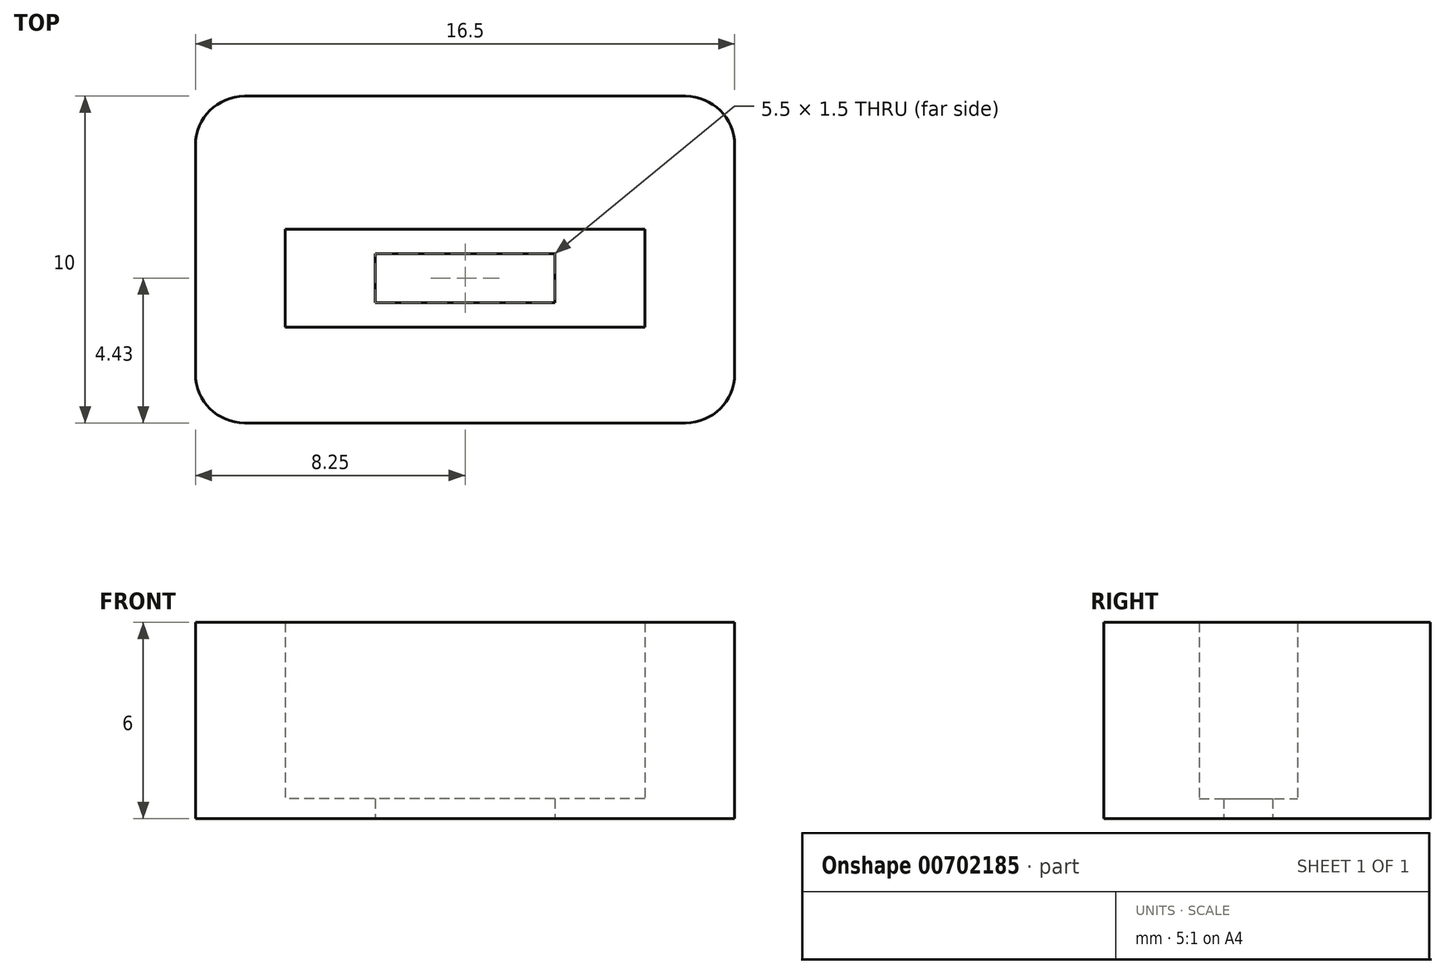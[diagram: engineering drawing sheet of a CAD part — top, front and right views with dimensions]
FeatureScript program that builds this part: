
annotation { "Feature Type Name" : "Feature", "Feature Type Description" : "" }
export const myFeature = defineFeature(function(context is Context, id is Id, definition is map)
    precondition{}
    {
        {
            var Q0;
            Q0=qCreatedBy(makeId("Top.planeOp"),FACE);
            var sketch = newSketch(context, id + "F0", { "sketchPlane" : qUnion([Q0])});
            skPoint(sketch, "E0.middle", {"position": v(0, 0) * mm});
            skLineSegment(sketch, "E1.top", {"start": v(1.25, 4.01) * mm, "end": v(-1.25, 4.01) * mm});
            skPoint(sketch, "E1.middle", {"position": v(0, 3.26) * mm});
            skPoint(sketch, "E1.middle.positionSnap0", {"position": v(0, 2.5) * mm});
            skPoint(sketch, "E1.centerSnap0", {"position": v(0, 2.5) * mm});
            skLineSegment(sketch, "E2.bottom", {"start": v(8.25, -4.43) * mm, "end": v(-8.25, -4.43) * mm});
            skLineSegment(sketch, "E2.top", {"start": v(8.25, 5.57) * mm, "end": v(-8.25, 5.57) * mm});
            skLineSegment(sketch, "E2.left", {"start": v(8.25, -4.43) * mm, "end": v(8.25, 5.57) * mm});
            skLineSegment(sketch, "E2.right", {"start": v(-8.25, -4.43) * mm, "end": v(-8.25, 5.57) * mm});
            skPoint(sketch, "E2.middle", {"position": v(0, 0.57) * mm});
            skLineSegment(sketch, "E3.bottom", {"start": v(5.5, -1.5) * mm, "end": v(-5.5, -1.5) * mm});
            skLineSegment(sketch, "E3.top", {"start": v(5.5, 1.5) * mm, "end": v(-5.5, 1.5) * mm});
            skLineSegment(sketch, "E3.left", {"start": v(5.5, -1.5) * mm, "end": v(5.5, 1.5) * mm});
            skLineSegment(sketch, "E3.right", {"start": v(-5.5, -1.5) * mm, "end": v(-5.5, 1.5) * mm});
            skLineSegment(sketch, "E4.bottom", {"start": v(2.75, -0.75) * mm, "end": v(-2.75, -0.75) * mm});
            skLineSegment(sketch, "E4.top", {"start": v(2.75, 0.75) * mm, "end": v(-2.75, 0.75) * mm});
            skLineSegment(sketch, "E4.left", {"start": v(2.75, -0.75) * mm, "end": v(2.75, 0.75) * mm});
            skLineSegment(sketch, "E4.right", {"start": v(-2.75, -0.75) * mm, "end": v(-2.75, 0.75) * mm});
            skSolve(sketch);
        }
        {
            var Q0;
            Q0=makeQuery(id+"F0.imprint","IMPRINT",FACE,{"disambiguationData":[TD([[makeQuery(id+"F0.imprint","IMPRINT",EDGE,{"derivedFrom":sQuery(id+"F0.wireOp",EDGE,"E2.bottom")}),-1.0]])]});
            extrude(context, id + "F1", {"entities" : qUnion([Q0]), "depth" : 6 * mm, "offsetDistance" : 25 * mm});
        }
        {
            var Q0;
            Q0=makeQuery(id+"F1.opExtrude","SWEPT_EDGE",EDGE,{"disambiguationData":[OSD([sQuery(id+"F0.wireOp",EDGE,"E2.top"),sQuery(id+"F0.wireOp",EDGE,"E2.right")])]});
            var Q1;
            Q1=makeQuery(id+"F1.opExtrude","SWEPT_EDGE",EDGE,{"disambiguationData":[OSD([sQuery(id+"F0.wireOp",EDGE,"E2.top"),sQuery(id+"F0.wireOp",EDGE,"E2.left")])]});
            var Q2;
            Q2=makeQuery(id+"F1.opExtrude","SWEPT_EDGE",EDGE,{"disambiguationData":[OSD([sQuery(id+"F0.wireOp",EDGE,"E2.bottom"),sQuery(id+"F0.wireOp",EDGE,"E2.left")])]});
            var Q3;
            Q3=makeQuery(id+"F1.opExtrude","SWEPT_EDGE",EDGE,{"disambiguationData":[OSD([sQuery(id+"F0.wireOp",EDGE,"E2.bottom"),sQuery(id+"F0.wireOp",EDGE,"E2.right")])]});
            fillet(context, id + "F2", {"entities" : qUnion([Q0, Q1, Q2, Q3]), "radius" : 1.5 * mm, "tangentPropagation" : true, "allowEdgeOverflow" : false});
        }
        {
            var Q0;
            Q0=makeQuery(id+"F0.imprint","IMPRINT",FACE,{"disambiguationData":[TD([[makeQuery(id+"F0.imprint","IMPRINT",EDGE,{"derivedFrom":sQuery(id+"F0.wireOp",EDGE,"E3.bottom")}),-1.0]])]});
            extrude(context, id + "F3", {"entities" : qUnion([Q0]), "operationType" : NewBodyOperationType.ADD, "depth" : 0.6 * mm, "offsetDistance" : 25 * mm});
        }
    });
